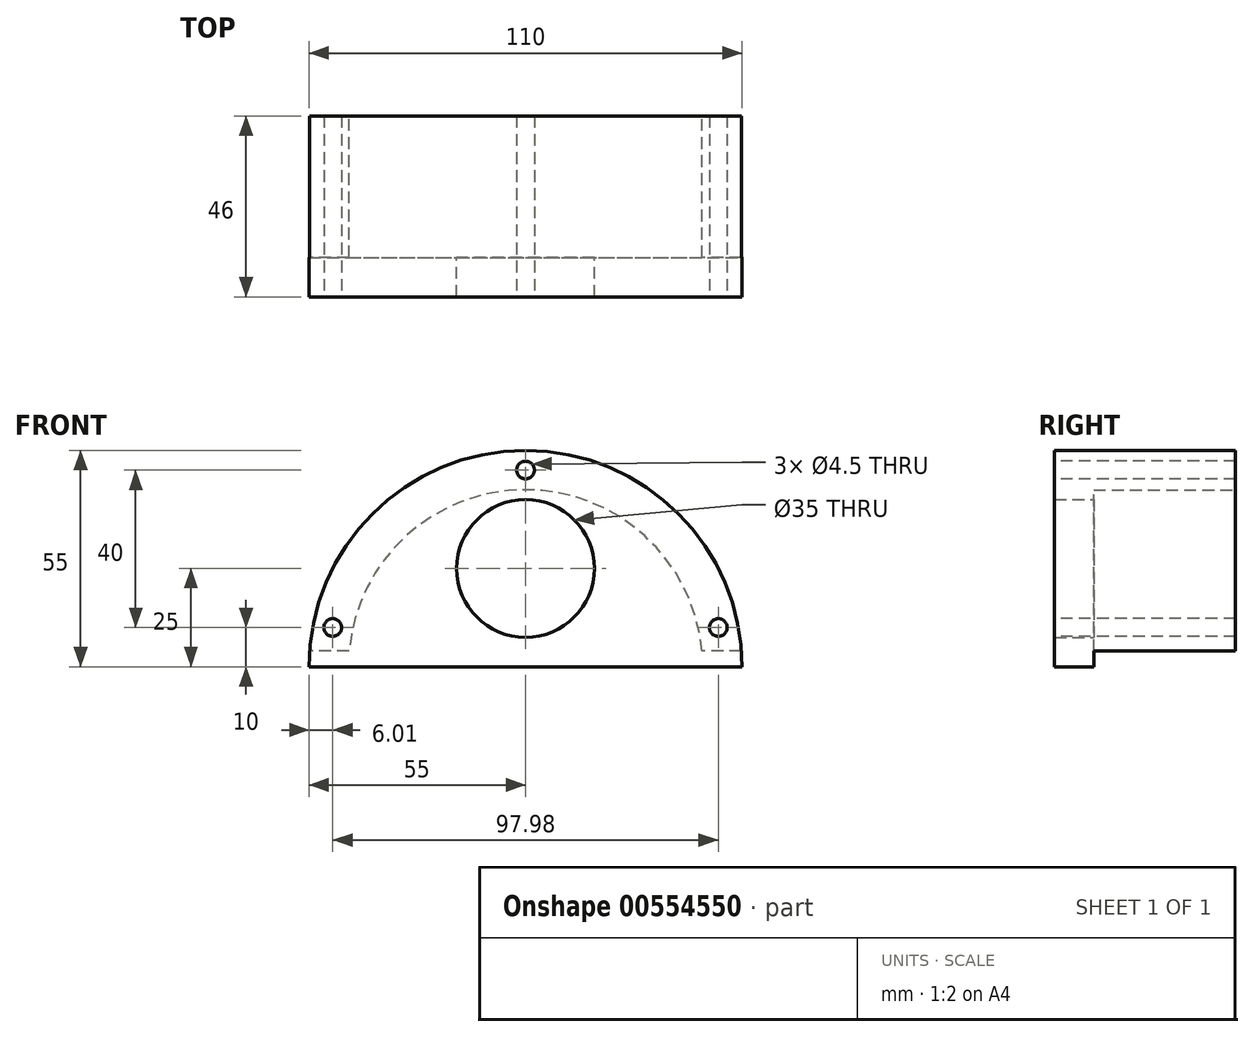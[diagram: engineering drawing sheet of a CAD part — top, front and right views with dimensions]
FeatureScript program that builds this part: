
annotation { "Feature Type Name" : "Feature", "Feature Type Description" : "" }
export const myFeature = defineFeature(function(context is Context, id is Id, definition is map)
    precondition{}
    {
        {
            var Q0;
            Q0=qCreatedBy(makeId("Front.planeOp"),FACE);
            var sketch = newSketch(context, id + "F0", { "sketchPlane" : qUnion([Q0])});
            skArc(sketch, "E0", {"start": v(55, 0) * mm, "mid": v(0, 55) * mm, "end": v(-55, 0) * mm});
            skLineSegment(sketch, "E1", {"start": v(-55, 0) * mm, "end": v(55, 0) * mm});
            skSolve(sketch);
        }
        {
            var Q0;
            Q0=makeQuery(id+"F0.imprint","IMPRINT",FACE,{"disambiguationData":[TD([[makeQuery(id+"F0.imprint","IMPRINT",EDGE,{"derivedFrom":sQuery(id+"F0.wireOp",EDGE,"E0")}),1.0]])]});
            extrude(context, id + "F1", {"entities" : qUnion([Q0]), "depth" : 46 * mm, "offsetDistance" : 25 * mm});
        }
        {
            var Q0;
            Q0=makeQuery(id+"F1.opExtrude","CAP_FACE",FACE,{"disambiguationData":[OSD([sQuery(id+"F0.wireOp",EDGE,"E0"),sQuery(id+"F0.wireOp",EDGE,"E1")])],"isStart":true});
            var sketch = newSketch(context, id + "F2", { "sketchPlane" : qUnion([Q0])});
            skCircle(sketch, "E2", {"center": v(0, 0) * mm, "radius": 45 * mm});
            skSolve(sketch);
        }
        {
            var Q0;
            {var subQ0=sQuery(id+"F2.wireOp",EDGE,"E2");var subQ1=makeQuery(id+"F1.opExtrude","CAP_EDGE",EDGE,{"disambiguationData":[OSD([sQuery(id+"F0.wireOp",EDGE,"E1")])],"isStart":true});var subQ2=makeQuery(id+"F2.imprint","INTERSECT",VERTEX,{"disambiguationData":[OD(0.0)],"derivedFrom":[subQ1,subQ0]});Q0=makeQuery(id+"F2.imprint","IMPRINT",FACE,{"disambiguationData":[TD([[makeQuery(id+"F2.imprint","IMPRINT",EDGE,{"disambiguationData":[TD([[subQ2,1.0]])],"derivedFrom":subQ0}),1.0]])]});}
            extrude(context, id + "F3", {"entities" : qUnion([Q0]), "operationType" : NewBodyOperationType.REMOVE, "oppositeDirection" : true, "depth" : 36 * mm, "offsetDistance" : 25 * mm});
        }
        {
            var Q0;
            Q0=qCreatedBy(makeId("Right.planeOp"),FACE);
            var sketch = newSketch(context, id + "F4", { "sketchPlane" : qUnion([Q0])});
            skLineSegment(sketch, "E3.bottom", {"start": v(0, 0) * mm, "end": v(-36, 0) * mm});
            skLineSegment(sketch, "E3.top", {"start": v(0, 4) * mm, "end": v(-36, 4) * mm});
            skLineSegment(sketch, "E3.left", {"start": v(0, 0) * mm, "end": v(0, 4) * mm});
            skLineSegment(sketch, "E3.right", {"start": v(-36, 0) * mm, "end": v(-36, 4) * mm});
            skSolve(sketch);
        }
        {
            var Q0;
            Q0=makeQuery(id+"F4.imprint","IMPRINT",FACE,{"disambiguationData":[TD([[makeQuery(id+"F4.imprint","IMPRINT",EDGE,{"derivedFrom":sQuery(id+"F4.wireOp",EDGE,"E3.bottom")}),-1.0]])]});
            extrude(context, id + "F5", {"entities" : qUnion([Q0]), "operationType" : NewBodyOperationType.REMOVE, "endBound" : BoundingType.SYMMETRIC, "depth" : 120 * mm, "offsetDistance" : 25 * mm});
        }
        {
            var Q0;
            Q0=makeQuery(id+"F3.boolean.opBoolean","COPY",FACE,{"derivedFrom":makeQuery(id+"F3.opExtrude","CAP_FACE",FACE,{"disambiguationData":[OSD([sQuery(id+"F0.wireOp",EDGE,"E1"),sQuery(id+"F2.wireOp",EDGE,"E2")])],"isStart":false})});
            var sketch = newSketch(context, id + "F6", { "sketchPlane" : qUnion([Q0])});
            skCircle(sketch, "E4", {"center": v(0, 25) * mm, "radius": 17.5 * mm});
            skLineSegment(sketch, "E5", {"start": v(0, 0) * mm, "end": v(0, 56.69) * mm});
            skSolve(sketch);
        }
        {
            var Q0;
            {var subQ0=sQuery(id+"F6.wireOp",EDGE,"E5");var subQ1=sQuery(id+"F6.wireOp",EDGE,"E4");var subQ2=makeQuery(id+"F6.imprint","INTERSECT",VERTEX,{"disambiguationData":[OD(0.0)],"derivedFrom":[subQ1,subQ0]});Q0=makeQuery(id+"F6.imprint","IMPRINT",FACE,{"disambiguationData":[TD([[makeQuery(id+"F6.imprint","IMPRINT",EDGE,{"disambiguationData":[TD([[subQ2,1.0]])],"derivedFrom":subQ1}),1.0]])]});}
            var Q1;
            {var subQ0=sQuery(id+"F6.wireOp",EDGE,"E5");var subQ1=sQuery(id+"F6.wireOp",EDGE,"E4");var subQ2=makeQuery(id+"F6.imprint","INTERSECT",VERTEX,{"disambiguationData":[OD(0.0)],"derivedFrom":[subQ1,subQ0]});Q1=makeQuery(id+"F6.imprint","IMPRINT",FACE,{"disambiguationData":[TD([[makeQuery(id+"F6.imprint","IMPRINT",EDGE,{"disambiguationData":[TD([[subQ2,-1.0]])],"derivedFrom":subQ1}),1.0]])]});}
            extrude(context, id + "F7", {"entities" : qUnion([Q0, Q1]), "operationType" : NewBodyOperationType.REMOVE, "oppositeDirection" : true, "depth" : 25 * mm, "offsetDistance" : 25 * mm});
        }
        {
            var Q0;
            Q0=makeQuery(id+"F1.opExtrude","CAP_FACE",FACE,{"disambiguationData":[OSD([sQuery(id+"F0.wireOp",EDGE,"E0"),sQuery(id+"F0.wireOp",EDGE,"E1")])],"isStart":false});
            var sketch = newSketch(context, id + "F8", { "sketchPlane" : qUnion([Q0])});
            skCircle(sketch, "E6", {"center": v(0, 0) * mm, "radius": 50 * mm});
            skPoint(sketch, "E7", {"position": v(48.99, 10) * mm});
            skPoint(sketch, "E8", {"position": v(-48.99, 10) * mm});
            skPoint(sketch, "E9", {"position": v(0, 50) * mm});
            skSolve(sketch);
        }
        {
            var Q0;
            Q0=sQuery(id+"F8.wireOp",VERTEX,"E7");
            var Q1;
            Q1=sQuery(id+"F8.wireOp",VERTEX,"E9");
            var Q2;
            Q2=sQuery(id+"F8.wireOp",VERTEX,"E8");
            var Q3;
            Q3=makeQuery(id+"F1.opExtrude","SWEPT_BODY",BODY,{"disambiguationData":[OSD([sQuery(id+"F0.wireOp",EDGE,"E0"),sQuery(id+"F0.wireOp",EDGE,"E1")])]});
            hole(context, id + "F9", {"style" : HoleStyle.SIMPLE, "endStyle" : HoleEndStyle.THROUGH, "holeDiameter" : 4.5 * mm, "isTappedThrough" : true, "tappedDepth" : 12 * mm, "tapClearance" : 3, "locations" : qUnion([Q0, Q1, Q2]), "scope" : qUnion([Q3])});
        }
    });
